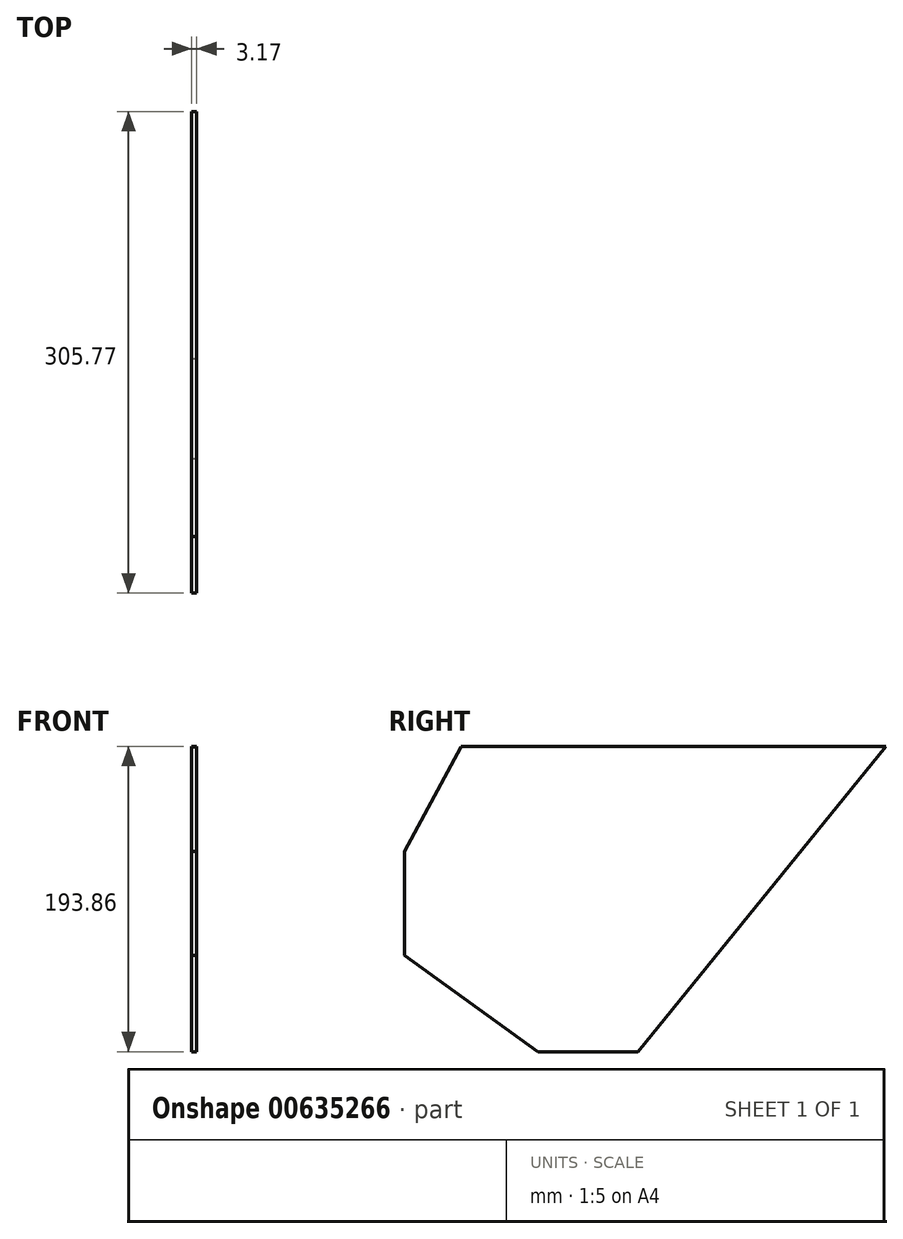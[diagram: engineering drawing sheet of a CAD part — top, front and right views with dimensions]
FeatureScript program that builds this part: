
annotation { "Feature Type Name" : "Feature", "Feature Type Description" : "" }
export const myFeature = defineFeature(function(context is Context, id is Id, definition is map)
    precondition{}
    {
        {
            var Q0;
            Q0=qCreatedBy(makeId("Right.planeOp"),FACE);
            var sketch = newSketch(context, id + "F0", { "sketchPlane" : qUnion([Q0])});
            skLineSegment(sketch, "E0.bottom", {"start": v(134.94, 118.28) * mm, "end": v(-134.94, 118.28) * mm});
            skLineSegment(sketch, "E0.right", {"start": v(-134.94, 118.28) * mm, "end": v(-134.94, -21.42) * mm});
            skPoint(sketch, "E0.middle", {"position": v(0, 0) * mm});
            skLineSegment(sketch, "E1", {"start": v(134.94, 118.28) * mm, "end": v(-22.34, -75.58) * mm});
            skLineSegment(sketch, "E2", {"start": v(-22.34, -75.58) * mm, "end": v(-85.84, -75.58) * mm});
            skLineSegment(sketch, "E3", {"start": v(-85.84, -75.58) * mm, "end": v(-77.84, -75.58) * mm});
            skLineSegment(sketch, "E4", {"start": v(-170.83, 51.54) * mm, "end": v(-134.94, 118.03) * mm});
            skLineSegment(sketch, "E5", {"start": v(-85.84, -75.58) * mm, "end": v(-170.83, -14.34) * mm});
            skLineSegment(sketch, "E6", {"start": v(-170.83, -14.34) * mm, "end": v(-170.83, 51.54) * mm});
            skSolve(sketch);
        }
        {
            var Q0;
            Q0 = qSketchRegion(id + "F0", true);
            extrude(context, id + "F1", {"entities" : qUnion([Q0]), "depth" : 3.17 * mm, "offsetDistance" : 25.4 * mm});
        }
    });
